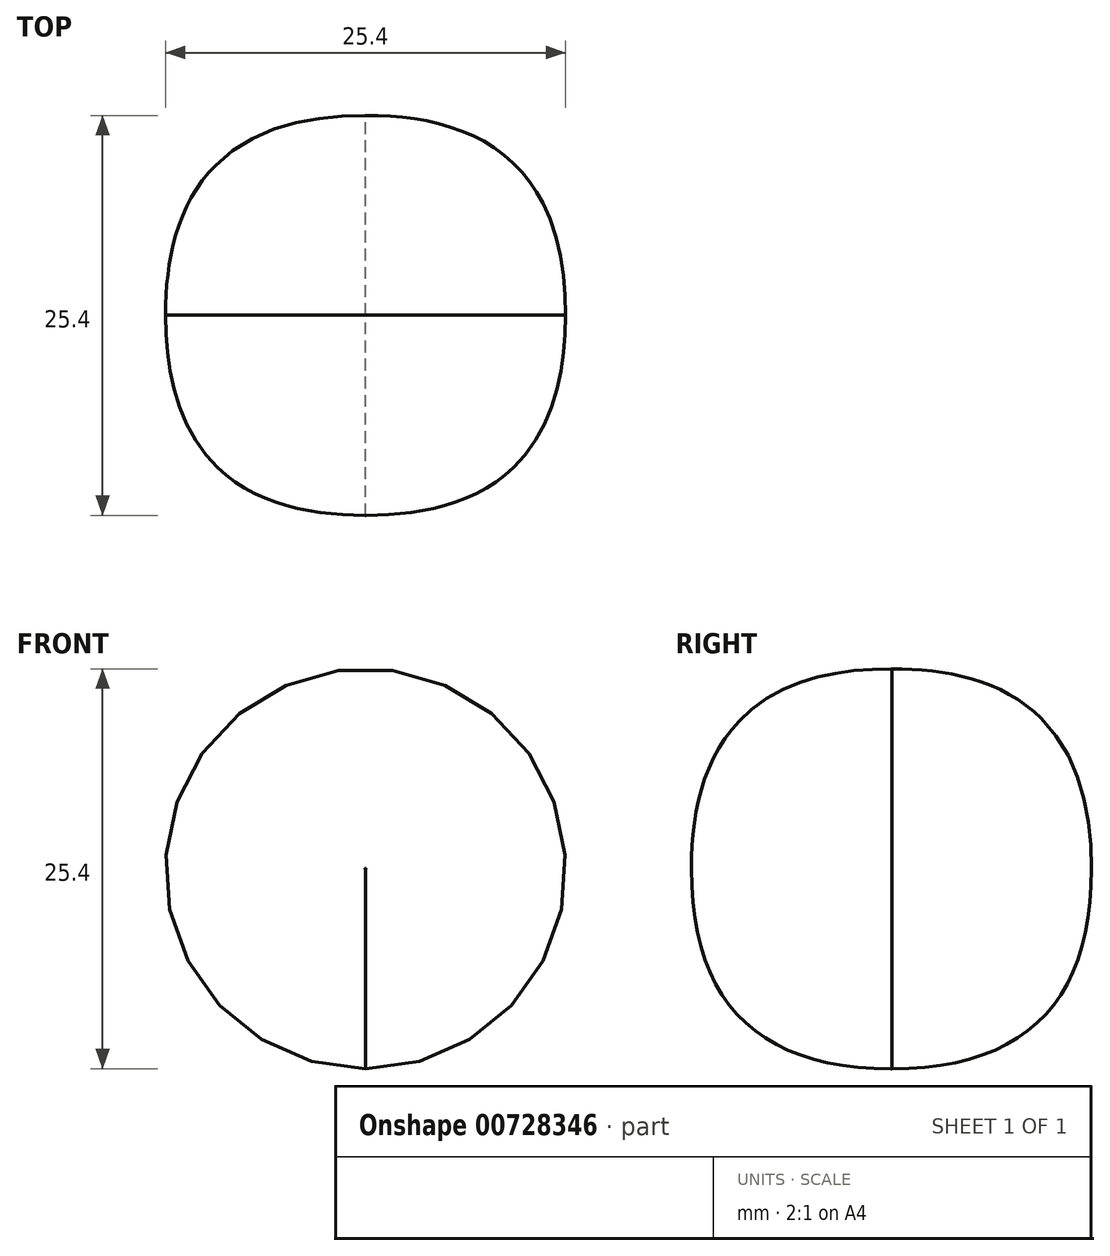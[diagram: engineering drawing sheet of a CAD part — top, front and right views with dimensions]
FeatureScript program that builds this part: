
annotation { "Feature Type Name" : "Feature", "Feature Type Description" : "" }
export const myFeature = defineFeature(function(context is Context, id is Id, definition is map)
    precondition{}
    {
        {
            var Q0;
            Q0=qCreatedBy(makeId("Front.planeOp"),FACE);
            var sketch = newSketch(context, id + "F0", { "sketchPlane" : qUnion([Q0])});
            skCircle(sketch, "E0", {"center": v(0, 0) * mm, "radius": 12.7 * mm});
            skSolve(sketch);
        }
        {
            var Q0;
            Q0=makeQuery(id+"F0.imprint","IMPRINT",FACE,{"disambiguationData":[TD([[makeQuery(id+"F0.imprint","IMPRINT",EDGE,{"derivedFrom":sQuery(id+"F0.wireOp",EDGE,"E0")}),1.0]])]});
            extrude(context, id + "F1", {"entities" : qUnion([Q0]), "depth" : 25.4 * mm, "offsetDistance" : 25.4 * mm});
        }
        {
            var Q0;
            Q0=makeQuery(id+"F1.opExtrude","CAP_EDGE",EDGE,{"disambiguationData":[OSD([sQuery(id+"F0.wireOp",EDGE,"E0")])],"isStart":false});
            var Q1;
            Q1=makeQuery(id+"F1.opExtrude","CAP_EDGE",EDGE,{"disambiguationData":[OSD([sQuery(id+"F0.wireOp",EDGE,"E0")])],"isStart":true});
            fillet(context, id + "F2", {"entities" : qUnion([Q0, Q1]), "radius" : 12.67 * mm, "tangentPropagation" : true, "rho" : 0.5, "crossSection" : FilletCrossSection.CONIC, "allowEdgeOverflow" : false});
        }
    });
